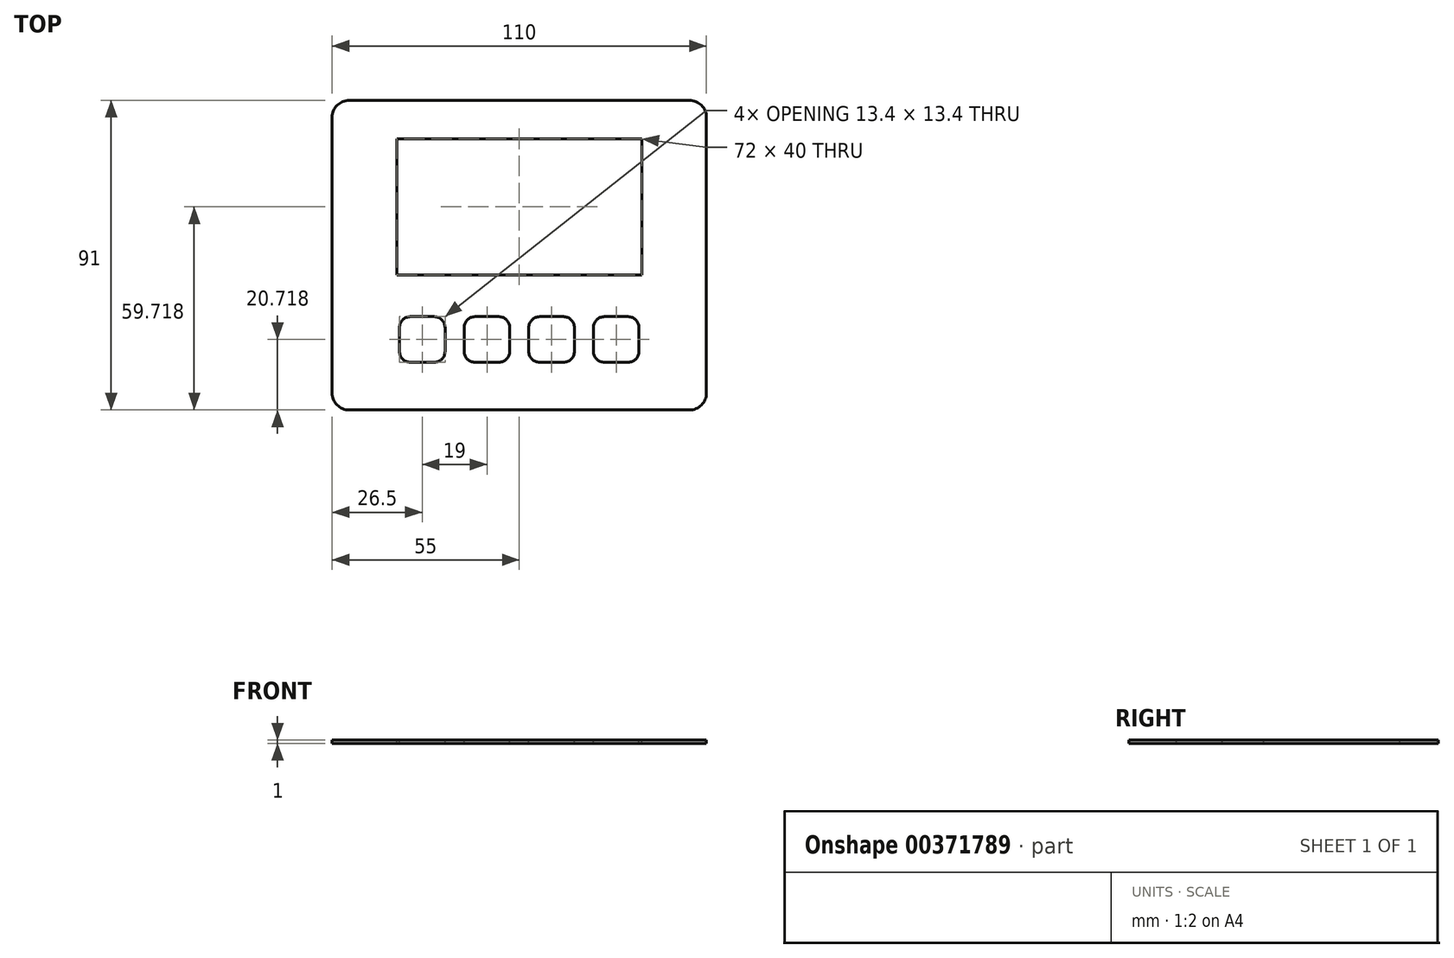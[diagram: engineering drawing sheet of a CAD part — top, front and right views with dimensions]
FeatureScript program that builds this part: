
annotation { "Feature Type Name" : "Feature", "Feature Type Description" : "" }
export const myFeature = defineFeature(function(context is Context, id is Id, definition is map)
    precondition{}
    {
        {
            var Q0;
            Q0=qCreatedBy(makeId("Top.planeOp"),FACE);
            var sketch = newSketch(context, id + "F0", { "sketchPlane" : qUnion([Q0])});
            skLineSegment(sketch, "E0.bottom", {"start": v(0, 0) * mm, "end": v(110, 0) * mm});
            skLineSegment(sketch, "E0.top", {"start": v(0, 91) * mm, "end": v(110, 91) * mm});
            skLineSegment(sketch, "E0.left", {"start": v(0, 0) * mm, "end": v(0, 91) * mm});
            skLineSegment(sketch, "E0.right", {"start": v(110, 0) * mm, "end": v(110, 91) * mm});
            skSolve(sketch);
        }
        {
            var Q0;
            Q0 = qSketchRegion(id + "F0", true);
            extrude(context, id + "F1", {"entities" : qUnion([Q0]), "depth" : 1 * mm});
        }
        {
            var Q0;
            Q0=makeQuery(id+"F1.opExtrude","CAP_FACE",FACE,{"disambiguationData":[OSD([sQuery(id+"F0.wireOp",EDGE,"E0.bottom"),sQuery(id+"F0.wireOp",EDGE,"E0.top"),sQuery(id+"F0.wireOp",EDGE,"E0.left"),sQuery(id+"F0.wireOp",EDGE,"E0.right")])],"isStart":false});
            var sketch = newSketch(context, id + "F2", { "sketchPlane" : qUnion([Q0])});
            skLineSegment(sketch, "E1.bottom", {"start": v(19, 79.72) * mm, "end": v(91, 79.72) * mm});
            skLineSegment(sketch, "E1.top", {"start": v(19, 39.72) * mm, "end": v(91, 39.72) * mm});
            skLineSegment(sketch, "E1.left", {"start": v(19, 79.72) * mm, "end": v(19, 39.72) * mm});
            skLineSegment(sketch, "E1.right", {"start": v(91, 79.72) * mm, "end": v(91, 39.72) * mm});
            skLineSegment(sketch, "E2", {"start": v(55, 91) * mm, "end": v(55, 79.72) * mm, "construction": true});
            skLineSegment(sketch, "E3", {"start": v(19, 79.72) * mm, "end": v(91, 39.72) * mm, "construction": true});
            skPoint(sketch, "E4", {"position": v(55, 59.72) * mm});
            skSolve(sketch);
        }
        {
            var Q0;
            Q0=makeQuery(id+"F2.imprint","IMPRINT",FACE,{"disambiguationData":[TD([[makeQuery(id+"F2.imprint","IMPRINT",EDGE,{"derivedFrom":sQuery(id+"F2.wireOp",EDGE,"E1.bottom")}),-1.0]])]});
            extrude(context, id + "F3", {"entities" : qUnion([Q0]), "operationType" : NewBodyOperationType.REMOVE, "endBound" : BoundingType.THROUGH_ALL, "oppositeDirection" : true, "depth" : 25 * mm});
        }
        {
            var Q0;
            Q0=makeQuery(id+"F1.opExtrude","SWEPT_EDGE",EDGE,{"disambiguationData":[OSD([sQuery(id+"F0.wireOp",EDGE,"E0.top"),sQuery(id+"F0.wireOp",EDGE,"E0.left")])]});
            var Q1;
            Q1=makeQuery(id+"F1.opExtrude","SWEPT_EDGE",EDGE,{"disambiguationData":[OSD([sQuery(id+"F0.wireOp",EDGE,"E0.bottom"),sQuery(id+"F0.wireOp",EDGE,"E0.left")])]});
            var Q2;
            Q2=makeQuery(id+"F1.opExtrude","SWEPT_EDGE",EDGE,{"disambiguationData":[OSD([sQuery(id+"F0.wireOp",EDGE,"E0.top"),sQuery(id+"F0.wireOp",EDGE,"E0.right")])]});
            var Q3;
            Q3=makeQuery(id+"F1.opExtrude","SWEPT_EDGE",EDGE,{"disambiguationData":[OSD([sQuery(id+"F0.wireOp",EDGE,"E0.bottom"),sQuery(id+"F0.wireOp",EDGE,"E0.right")])]});
            fillet(context, id + "F4", {"entities" : qUnion([Q0, Q1, Q2, Q3]), "radius" : 5 * mm, "tangentPropagation" : true, "allowEdgeOverflow" : false});
        }
        {
            var Q0;
            Q0=makeQuery(id+"F1.opExtrude","CAP_FACE",FACE,{"disambiguationData":[OSD([sQuery(id+"F0.wireOp",EDGE,"E0.bottom"),sQuery(id+"F0.wireOp",EDGE,"E0.top"),sQuery(id+"F0.wireOp",EDGE,"E0.left"),sQuery(id+"F0.wireOp",EDGE,"E0.right")])],"isStart":false});
            var sketch = newSketch(context, id + "F5", { "sketchPlane" : qUnion([Q0])});
            skLineSegment(sketch, "E5.bottom", {"start": v(23, 27.42) * mm, "end": v(30, 27.42) * mm});
            skLineSegment(sketch, "E5.top", {"start": v(23, 14.02) * mm, "end": v(30, 14.02) * mm});
            skLineSegment(sketch, "E5.left", {"start": v(19.8, 24.22) * mm, "end": v(19.8, 17.22) * mm});
            skLineSegment(sketch, "E5.right", {"start": v(33.2, 24.22) * mm, "end": v(33.2, 17.22) * mm});
            skPoint(sketch, "E6.visualSharp", {"position": v(19.8, 27.42) * mm});
            skArc(sketch, "E6.filletArc", {"start": v(23, 27.42) * mm, "mid": v(20.74, 26.48) * mm, "end": v(19.8, 24.22) * mm});
            skPoint(sketch, "E7.visualSharp", {"position": v(33.2, 27.42) * mm});
            skArc(sketch, "E7.filletArc", {"start": v(33.2, 24.22) * mm, "mid": v(32.26, 26.48) * mm, "end": v(30, 27.42) * mm});
            skPoint(sketch, "E8.visualSharp", {"position": v(33.2, 14.02) * mm});
            skArc(sketch, "E8.filletArc", {"start": v(30, 14.02) * mm, "mid": v(32.26, 14.96) * mm, "end": v(33.2, 17.22) * mm});
            skPoint(sketch, "E9.visualSharp", {"position": v(19.8, 14.02) * mm});
            skArc(sketch, "E9.filletArc", {"start": v(19.8, 17.22) * mm, "mid": v(20.74, 14.96) * mm, "end": v(23, 14.02) * mm});
            skLineSegment(sketch, "E10.1.0.0", {"start": v(42, 27.42) * mm, "end": v(49, 27.42) * mm});
            skArc(sketch, "E10.1.0.1", {"start": v(42, 27.42) * mm, "mid": v(39.74, 26.48) * mm, "end": v(38.8, 24.22) * mm});
            skLineSegment(sketch, "E10.1.0.2", {"start": v(38.8, 24.22) * mm, "end": v(38.8, 17.22) * mm});
            skArc(sketch, "E10.1.0.3", {"start": v(38.8, 17.22) * mm, "mid": v(39.74, 14.96) * mm, "end": v(42, 14.02) * mm});
            skLineSegment(sketch, "E10.1.0.4", {"start": v(42, 14.02) * mm, "end": v(49, 14.02) * mm});
            skArc(sketch, "E10.1.0.5", {"start": v(49, 14.02) * mm, "mid": v(51.26, 14.96) * mm, "end": v(52.2, 17.22) * mm});
            skArc(sketch, "E10.1.0.6", {"start": v(52.2, 24.22) * mm, "mid": v(51.26, 26.48) * mm, "end": v(49, 27.42) * mm});
            skLineSegment(sketch, "E10.1.0.7", {"start": v(52.2, 24.22) * mm, "end": v(52.2, 17.22) * mm});
            skLineSegment(sketch, "E10.2.0.0", {"start": v(61, 27.42) * mm, "end": v(68, 27.42) * mm});
            skArc(sketch, "E10.2.0.1", {"start": v(61, 27.42) * mm, "mid": v(58.74, 26.48) * mm, "end": v(57.8, 24.22) * mm});
            skLineSegment(sketch, "E10.2.0.2", {"start": v(57.8, 24.22) * mm, "end": v(57.8, 17.22) * mm});
            skArc(sketch, "E10.2.0.3", {"start": v(57.8, 17.22) * mm, "mid": v(58.74, 14.96) * mm, "end": v(61, 14.02) * mm});
            skLineSegment(sketch, "E10.2.0.4", {"start": v(61, 14.02) * mm, "end": v(68, 14.02) * mm});
            skArc(sketch, "E10.2.0.5", {"start": v(68, 14.02) * mm, "mid": v(70.26, 14.96) * mm, "end": v(71.2, 17.22) * mm});
            skArc(sketch, "E10.2.0.6", {"start": v(71.2, 24.22) * mm, "mid": v(70.26, 26.48) * mm, "end": v(68, 27.42) * mm});
            skLineSegment(sketch, "E10.2.0.7", {"start": v(71.2, 24.22) * mm, "end": v(71.2, 17.22) * mm});
            skLineSegment(sketch, "E10.3.0.0", {"start": v(80, 27.42) * mm, "end": v(87, 27.42) * mm});
            skArc(sketch, "E10.3.0.1", {"start": v(80, 27.42) * mm, "mid": v(77.74, 26.48) * mm, "end": v(76.8, 24.22) * mm});
            skLineSegment(sketch, "E10.3.0.2", {"start": v(76.8, 24.22) * mm, "end": v(76.8, 17.22) * mm});
            skArc(sketch, "E10.3.0.3", {"start": v(76.8, 17.22) * mm, "mid": v(77.74, 14.96) * mm, "end": v(80, 14.02) * mm});
            skLineSegment(sketch, "E10.3.0.4", {"start": v(80, 14.02) * mm, "end": v(87, 14.02) * mm});
            skArc(sketch, "E10.3.0.5", {"start": v(87, 14.02) * mm, "mid": v(89.26, 14.96) * mm, "end": v(90.2, 17.22) * mm});
            skArc(sketch, "E10.3.0.6", {"start": v(90.2, 24.22) * mm, "mid": v(89.26, 26.48) * mm, "end": v(87, 27.42) * mm});
            skLineSegment(sketch, "E10.3.0.7", {"start": v(90.2, 24.22) * mm, "end": v(90.2, 17.22) * mm});
            skLineSegment(sketch, "E10.direction1", {"start": v(23, 27.42) * mm, "end": v(42, 27.42) * mm, "construction": true});
            skLineSegment(sketch, "E11", {"start": v(19.8, 20.72) * mm, "end": v(90.2, 20.72) * mm, "construction": true});
            skPoint(sketch, "E12", {"position": v(55, 20.72) * mm});
            skLineSegment(sketch, "E13", {"start": v(55, 39.72) * mm, "end": v(55, 20.72) * mm, "construction": true});
            skSolve(sketch);
        }
        {
            var Q0;
            Q0 = qSketchRegion(id + "F5", true);
            extrude(context, id + "F6", {"entities" : qUnion([Q0]), "operationType" : NewBodyOperationType.REMOVE, "endBound" : BoundingType.THROUGH_ALL, "oppositeDirection" : true, "depth" : 25 * mm});
        }
    });
